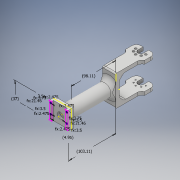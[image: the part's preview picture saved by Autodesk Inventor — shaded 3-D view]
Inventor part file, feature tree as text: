
AUTODESK INVENTOR PART (.ipt)
format: ipt  version: 2018 (Build 220112000, 112)  size: 543,744 bytes
history: native  units: mm
features: sketch x23, extrude x22, projected_geometry x18, fillet x6, other x1
ambient origin geometry x8: Origin, YZ Plane, XZ Plane, XY Plane, X Axis, Y Axis, Z Axis, Center Point
bodies: Body1 (feature_tree)
feature tree (70):
  other  "Sólido1"
  extrude  "Extrusión1"  Depth=29.0mm
  extrude  "Extrusión2"  Depth=26.0mm
  extrude  "Extrusión3"  Depth=29.0mm
  extrude  "Extrusión4"  Depth=29.0mm
  extrude  "Extrusión5"  Depth=7.5mm TaperAngle=0.0deg
  extrude  "Extrusión6"  Depth=7.5mm
  fillet  "Empalme1"  Radius=7.5mm
  fillet  "Empalme2"  Radius=7.5mm
  extrude  "Extrusión7"  Depth=10.0mm
  extrude  "Extrusión8"  Depth=10.0mm
  extrude  "Extrusión14"  Depth=29.0mm TaperAngle=0.0deg
  extrude  "Extrusión15"  Depth=103.11mm TaperAngle=0.0deg
  extrude  "Extrusión16"  Depth=10.0mm
  extrude  "Extrusión17"  Depth=29.0mm
  extrude  "Extrusión18"  Depth=10.0mm
  extrude  "Extrusión19"  Depth=5.0mm
  extrude  "Extrusión20"  Depth=2.7mm
  sketch  "Boceto21"  dims[d39=4.8mm d40=2.7mm]
  sketch  "Boceto22"  dims[d41=2.7mm d43=11.15mm]
  extrude  "Extrusión23"  Depth=2.7mm
  extrude  "Extrusión24"  Depth=11.15mm
  extrude  "Extrusión25"  Depth=11.15mm
  fillet  "Empalme7"  Radius=2.7mm
  fillet  "Empalme8"  Radius=2.7mm
  sketch  "Boceto26"  dims[d55=28.0mm d57=4.0mm d58=0.0mm]
  extrude  "Extrusión26"  Depth=11.15mm
  fillet  "Empalme9"  Radius=67.0mm
  extrude  "Extrusión27"  Depth=40.25mm
  extrude  "Extrusión28"  Depth=4.0mm TaperAngle=0.0deg
  extrude  "Extrusión29"  Depth=21.1mm
  sketch  "Boceto29"  dims[d92=4.8mm d93=4.8mm d94=4.8mm d95=4.8mm d96=5.5mm d97=0.0mm d98=5.5mm d99=0.0mm d100=13.0mm d101=5.0mm d102=0.0mm d103=37.0mm d104=4.95mm d105=37.0mm d106=4.95mm d107=4.0mm d108=0.0mm d109=4.95mm d110=0.0mm d111=40.5mm d112=0.0mm d113=4.95mm d114=0.0mm d115=3.5mm d116=3.75mm d117=3.75mm d118=2.475mm d119=2.475mm d120=3.5mm d121=3.5mm d122=3.5mm d123=21.46mm d124=21.46mm d125=2.475mm d126=2.475mm d129=4.95mm d135=5.0mm d136=3.129506mm d137=3.129506mm d139=67.0mm d140=0.0mm d141=6.370494mm d142=6.370494mm d143=6.370494mm d144=6.370494mm d145=6.370494mm d146=6.370494mm d147=6.370494mm d148=24.0mm d149=6.370494mm d150=24.0mm d151=7.5mm d152=0.0mm d153=7.5mm d154=0.0mm d155=10.0mm d156=10.0mm d157=5.0mm d158=0.0mm d159=3.0mm d160=13.0mm d161=0.0mm d162=11.370494mm d163=11.370494mm d164=2.0mm d165=2.0mm d166=11.370494mm d167=11.370494mm d168=7.5mm d169=0.0mm d170=7.5mm d171=0.0mm d172=37.0mm d173=98.11mm d174=103.11mm d175=3.0mm]
  fillet  "Empalme10"  Radius=4.8mm
  sketch  "Boceto1"  dims[d0=52.0mm d1=29.0mm]
  sketch  "Boceto2"  dims[d2=14.5mm d3=26.0mm]
  projected_geometry  "Contorno proyectado1"
  sketch  "Boceto3"  dims[d4=7.5mm d5=0.0mm d6=29.0mm]
  projected_geometry  "Contorno proyectado2"
  projected_geometry  "Contorno proyectado3"
  sketch  "Boceto4"  dims[d7=67.0mm d8=29.0mm]
  sketch  "Boceto5"  dims[d9=7.5mm d10=0.0mm d11=7.5mm d12=0.0mm]
  sketch  "Boceto6"  dims[d13=7.5mm d14=7.5mm d15=7.5mm d16=7.5mm]
  sketch  "Boceto7"  dims[d17=29.0mm d18=0.0mm d19=10.0mm]
  projected_geometry  "Contorno proyectado5"
  sketch  "Boceto8"  dims[d20=10.0mm d21=10.0mm]
  projected_geometry  "Contorno proyectado6"
  sketch  "Boceto14"  dims[d22=10.0mm d23=29.0mm d24=0.0mm]
  sketch  "Boceto15"  dims[d26=28.0mm d27=103.11mm d28=0.0mm]
  sketch  "Boceto16"  dims[d29=10.0mm d30=10.0mm]
  sketch  "Boceto17"  dims[d31=29.0mm d32=74.5mm]
  projected_geometry  "Contorno proyectado12"
  sketch  "Boceto18"  dims[d33=14.5mm d34=10.0mm]
  projected_geometry  "Contorno proyectado13"
  sketch  "Boceto19"  dims[d35=5.0mm d36=5.0mm]
  projected_geometry  "Contorno proyectado14"
  sketch  "Boceto20"  dims[d37=5.0mm d38=2.7mm]
  projected_geometry  "Contorno proyectado15"
  projected_geometry  "Contorno proyectado16"
  projected_geometry  "Contorno proyectado17"
  projected_geometry  "Contorno proyectado18"
  sketch  "Boceto23"  dims[d44=11.15mm d45=11.15mm d46=2.7mm d47=2.7mm]
  projected_geometry  "Contorno proyectado19"
  sketch  "Boceto24"  dims[d48=11.15mm d49=11.15mm d50=67.0mm d51=0.0mm]
  projected_geometry  "Contorno proyectado20"
  sketch  "Boceto25"  dims[d52=40.25mm d53=40.25mm]
  projected_geometry  "Contorno proyectado21"
  projected_geometry  "Contorno proyectado22"
  projected_geometry  "Contorno proyectado23"
  projected_geometry  "Contorno proyectado24"
  sketch  "Boceto28"  dims[d89=20.125mm d90=21.1mm d91=4.8mm]
